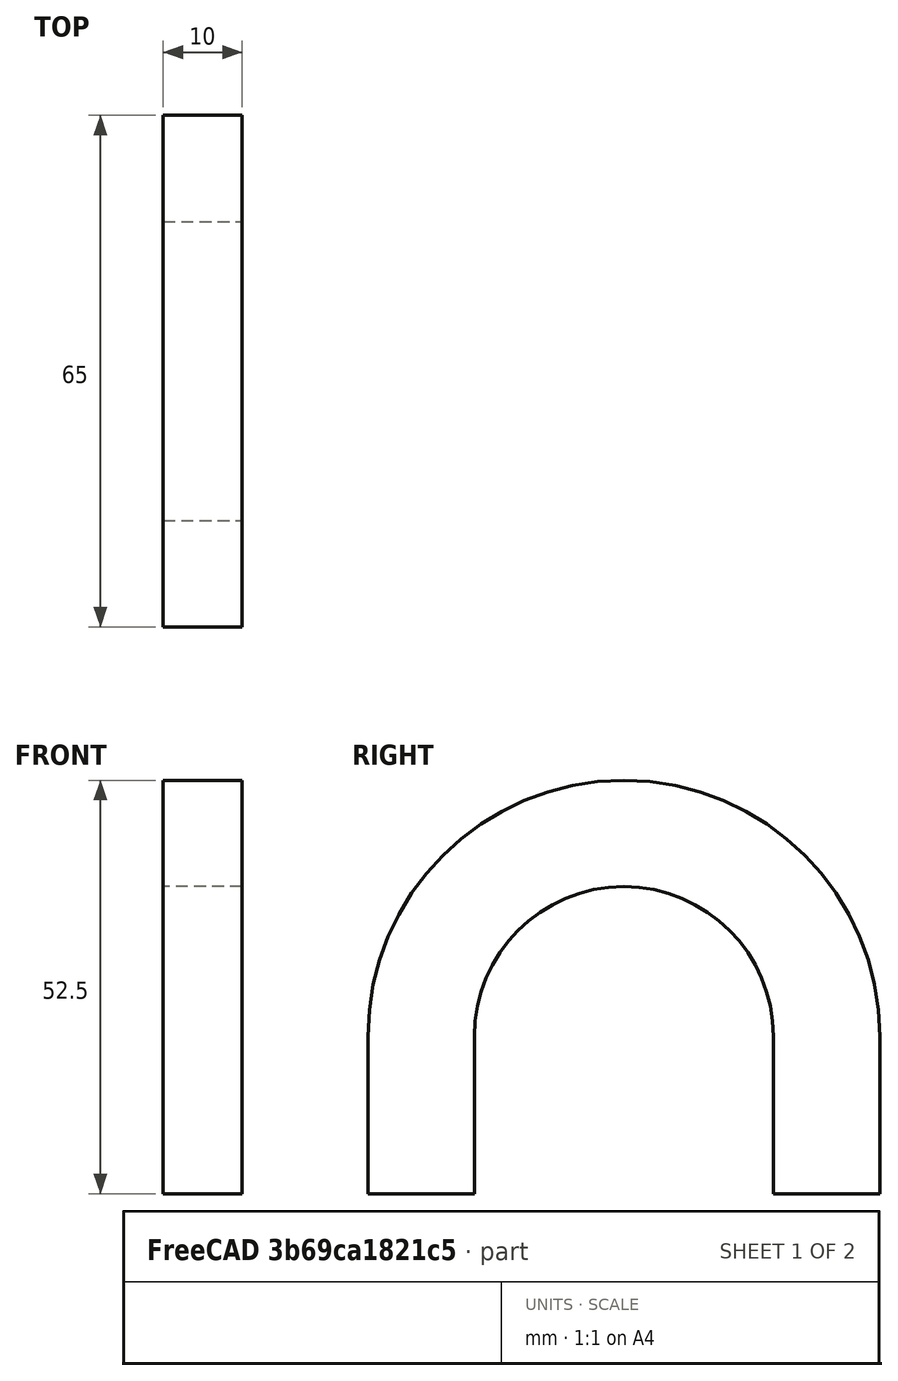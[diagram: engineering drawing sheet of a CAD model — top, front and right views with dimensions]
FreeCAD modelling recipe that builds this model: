
FCSTD DOCUMENT  (FreeCAD 0.15R4671 (Git))
Label: rain_cover_positioning_pattern
License: All rights reserved
LicenseURL: http://en.wikipedia.org/wiki/All_rights_reserved
objects: Sketcher::SketchObject×1, PartDesign::Pad×1, Drawing::FeatureViewPart×1, Drawing::FeaturePage×1
note: 3 computed .brp shape members not serialized (recipe doc carries the construction recipe); baked Part::Feature solids carry a one-line shape summary decoded from their .brp

FEATURE [Sketcher::SketchObject] Sketch
  Placement = pos=(0,0,0) rot=(0.57735,0.57735,0.57735;2.0944rad)
  sketch-geometry (8):
    g0: ArcOfCircle CenterX=0 CenterY=0 CenterZ=0 NormalX=0 NormalY=0 NormalZ=1 Radius=32.5 StartAngle=6.28319 EndAngle=9.42478
    g1: LineSegment StartX=32.5 StartY=-2.88064e-07 StartZ=0 EndX=32.5 EndY=-20 EndZ=0
    g2: LineSegment StartX=32.5 StartY=-20 StartZ=0 EndX=19 EndY=-20 EndZ=0
    g3: LineSegment StartX=-32.5 StartY=-20 StartZ=0 EndX=-32.5 EndY=2.47343e-07 EndZ=0
    g4: LineSegment StartX=-19 StartY=-20 StartZ=0 EndX=-19 EndY=-1.0109e-07 EndZ=0
    g5: LineSegment StartX=19 StartY=8.73553e-07 StartZ=0 EndX=19 EndY=-20 EndZ=0
    g6: LineSegment StartX=-19 StartY=-20 StartZ=0 EndX=-32.5 EndY=-20 EndZ=0
    g7: ArcOfCircle CenterX=0 CenterY=0 CenterZ=0 NormalX=0 NormalY=0 NormalZ=1 Radius=19 StartAngle=4.5976e-08 EndAngle=3.14159
  constraints (23):
    c: Coincident(g1,g2)
    c: Coincident(g6,g3)
    c: Horizontal(g2)
    c: Vertical(g1)
    c: Vertical(g3)
    c: Tangent(g3,g0)
    c: Tangent(g1,g0)
    c: Coincident(g0,g-1)
    c: Coincident(g0,g1)
    c: Coincident(g0,g3)
    c: Vertical(g4)
    c: Vertical(g5)
    c: Coincident(g5,g2)
    c: Coincident(g4,g6)
    c: Coincident(g7,g4)
    c: Coincident(g7,g5)
    c: Tangent(g7,g4)
    c: Coincident(g-1,g7)
    c: Radius(g7) = 19
    c: Symmetric(g4,g2,g-2)
    c: Horizontal(g6)
    c: DistanceY(g4) = 20
    c: DistanceX(g-1,g3) = -32.5
FEATURE [PartDesign::Pad] Pad
  Length = 10
  Length2 = 100
  Placement = pos=(0,0,0) rot=(0.57735,0.57735,0.57735;2.0944rad)
  Sketch = -> Sketch
  Type = 0
FEATURE [Drawing::FeatureViewPart] Ortho  label="Ortho_0_0"
  Direction = (1,0,0)
  HiddenWidth = 0.15
  LineWidth = 0.35
  Rotation = -90
  ShowHiddenLines = false
  ShowSmoothLines = false
  Source = -> Pad
  Tolerance = 0.05
  ViewResult = <g id="Ortho_0_0"\n   transform="rotate(-90,105,154.75) translate(105,154.75) scale(1,1)"\n  >\n<g   stroke="rgb(0, 0, 0)"\n   stroke-width="0.35"\n   stroke-linecap="butt"\n   stroke-linejoin="miter"\n   fill="none"\n   transform="scale(1,-1)"\n  >\n<path id= "1" d=" M 8.73553e-07 -19 L -20 -19 " />\n<path id= "2" d=" M -20 -32.5 L -20 -19 " />\n<path id= "3" d=" M -2.88064e-07 -32.5 L -20 -32.5 " />\n<path d="M-2.88064e-07 -32.5 A32.5 32.5 0 1 1 2.47343e-07 32.5" /><path id= "5" d=" M -20 32.5 L 2.47343e-07 32.5 " />\n<path id= "6" d=" M -20 19 L -20 32.5 " />\n<path id= "7" d=" M -20 19 L -1.0109e-07 19 " />\n<path d="M8.73553e-07 -19 A19 19 0 0 1 -1.0109e-07 19" /></g>\n</g>
  Visible = true
  X = 105
  Y = 154.75
FEATURE [Drawing::FeaturePage] Page
  Group = -> [Ortho]
  Template = <path>
note: 1 file-system path scrubbed to <path> (originals preserved in the JSON sidecar)
